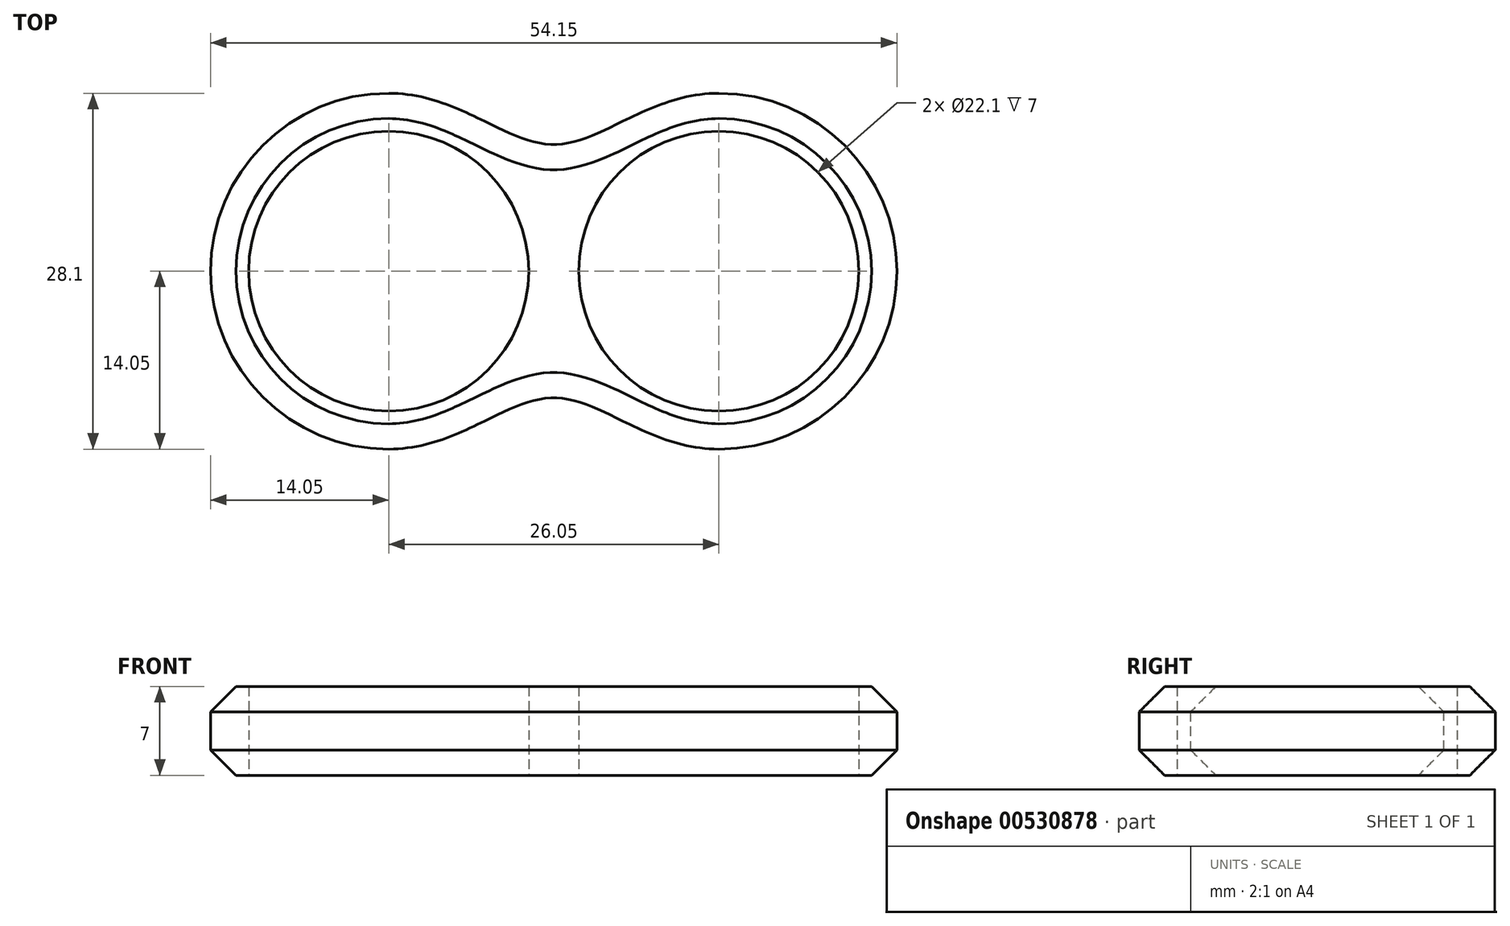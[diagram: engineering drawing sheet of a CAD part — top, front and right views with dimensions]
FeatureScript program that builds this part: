
annotation { "Feature Type Name" : "Feature", "Feature Type Description" : "" }
export const myFeature = defineFeature(function(context is Context, id is Id, definition is map)
    precondition{}
    {
        {
            var Q0;
            Q0=qCreatedBy(makeId("Top.planeOp"),FACE);
            var sketch = newSketch(context, id + "F0", { "sketchPlane" : qUnion([Q0])});
            skCircle(sketch, "E0", {"center": v(0, 0) * mm, "radius": 11 * mm, "construction": true});
            skCircle(sketch, "E1.0", {"center": v(0, 0) * mm, "radius": 11.05 * mm});
            skLineSegment(sketch, "E2", {"start": v(-11.05, 0) * mm, "end": v(-26.05, 0) * mm, "construction": true});
            skCircle(sketch, "E3", {"center": v(-26.05, 0) * mm, "radius": 11 * mm, "construction": true});
            skCircle(sketch, "E4.0", {"center": v(-26.05, 0) * mm, "radius": 11.05 * mm});
            skCircle(sketch, "E5.0", {"center": v(0, 0) * mm, "radius": 14.05 * mm});
            skCircle(sketch, "E6.0", {"center": v(-26.05, 0) * mm, "radius": 14.05 * mm});
            skLineSegment(sketch, "E7", {"start": v(-11.05, 0) * mm, "end": v(-15, 0) * mm, "construction": true});
            skLineSegment(sketch, "E8", {"start": v(-13.03, 10) * mm, "end": v(-13.03, -10) * mm, "construction": true});
            skPoint(sketch, "E9", {"position": v(-13.03, 0) * mm});
            skFitSpline(sketch, "E10", {"points": [v(-26.05, -14.05) * mm, v(-13.03, -10) * mm, v(0, -14.05) * mm], "startDerivative": vector(33.15, 0) * mm, "endDerivative": vector(33.15, 0) * mm});
            skLineSegment(sketch, "E11", {"start": v(-20.52, -10) * mm, "end": v(-5.53, -10) * mm, "construction": true});
            skLineSegment(sketch, "E12.MirrorCS", {"start": v(-20.52, 10) * mm, "end": v(-5.53, 10) * mm, "construction": true});
            skFitSpline(sketch, "E13.MirrorCS", {"points": [v(-26.05, 14.05) * mm, v(-13.03, 10) * mm, v(0, 14.05) * mm], "startDerivative": vector(33.15, 0) * mm, "endDerivative": vector(33.15, 0) * mm});
            skSolve(sketch);
        }
        {
            var Q0;
            Q0=makeQuery(id+"F0.imprint","IMPRINT",FACE,{"disambiguationData":[TD([[makeQuery(id+"F0.imprint","IMPRINT",EDGE,{"derivedFrom":sQuery(id+"F0.wireOp",EDGE,"E4.0")}),-1.0]])]});
            var Q1;
            {var subQ0=sQuery(id+"F0.wireOp",EDGE,"E10");Q1=makeQuery(id+"F0.imprint","IMPRINT",FACE,{"disambiguationData":[TD([[makeQuery(id+"F0.imprint","IMPRINT",EDGE,{"derivedFrom":subQ0}),1.0]])]});}
            var Q2;
            Q2=makeQuery(id+"F0.imprint","IMPRINT",FACE,{"disambiguationData":[TD([[makeQuery(id+"F0.imprint","IMPRINT",EDGE,{"derivedFrom":sQuery(id+"F0.wireOp",EDGE,"E1.0")}),-1.0]])]});
            var Q3;
            {var subQ0=sQuery(id+"F0.wireOp",EDGE,"E13.MirrorCS");var subQ1=sQuery(id+"F0.wireOp",EDGE,"E5.0");var subQ2=makeQuery(id+"F0.imprint","INTERSECT",VERTEX,{"disambiguationData":[OD(1.0)],"derivedFrom":[subQ1,subQ0]});Q3=makeQuery(id+"F0.imprint","IMPRINT",FACE,{"disambiguationData":[TD([[makeQuery(id+"F0.imprint","IMPRINT",EDGE,{"disambiguationData":[TD([[subQ2,-1.0]])],"derivedFrom":subQ1}),-1.0]])]});}
            var Q4;
            {var subQ0=sQuery(id+"F0.wireOp",EDGE,"E6.0");var subQ1=sQuery(id+"F0.wireOp",EDGE,"E5.0");var subQ2=makeQuery(id+"F0.imprint","INTERSECT",VERTEX,{"disambiguationData":[OD(0.0)],"derivedFrom":[subQ1,subQ0]});Q4=makeQuery(id+"F0.imprint","IMPRINT",FACE,{"disambiguationData":[TD([[makeQuery(id+"F0.imprint","IMPRINT",EDGE,{"disambiguationData":[TD([[subQ2,-1.0]])],"derivedFrom":subQ1}),1.0]])]});}
            extrude(context, id + "F1", {"entities" : qUnion([Q0, Q1, Q2, Q3, Q4]), "depth" : 7 * mm, "offsetDistance" : 25 * mm});
        }
        {
            var Q0;
            Q0=makeQuery(id+"F1.opExtrude","CAP_EDGE",EDGE,{"disambiguationData":[OSD([sQuery(id+"F0.wireOp",EDGE,"E10")])],"isStart":false});
            var Q1;
            Q1=makeQuery(id+"F1.opExtrude","CAP_EDGE",EDGE,{"disambiguationData":[OSD([sQuery(id+"F0.wireOp",EDGE,"E10")])],"isStart":true});
            chamfer(context, id + "F2", {"entities" : qUnion([Q0, Q1]), "width" : 2 * mm, "tangentPropagation" : true});
        }
    });
